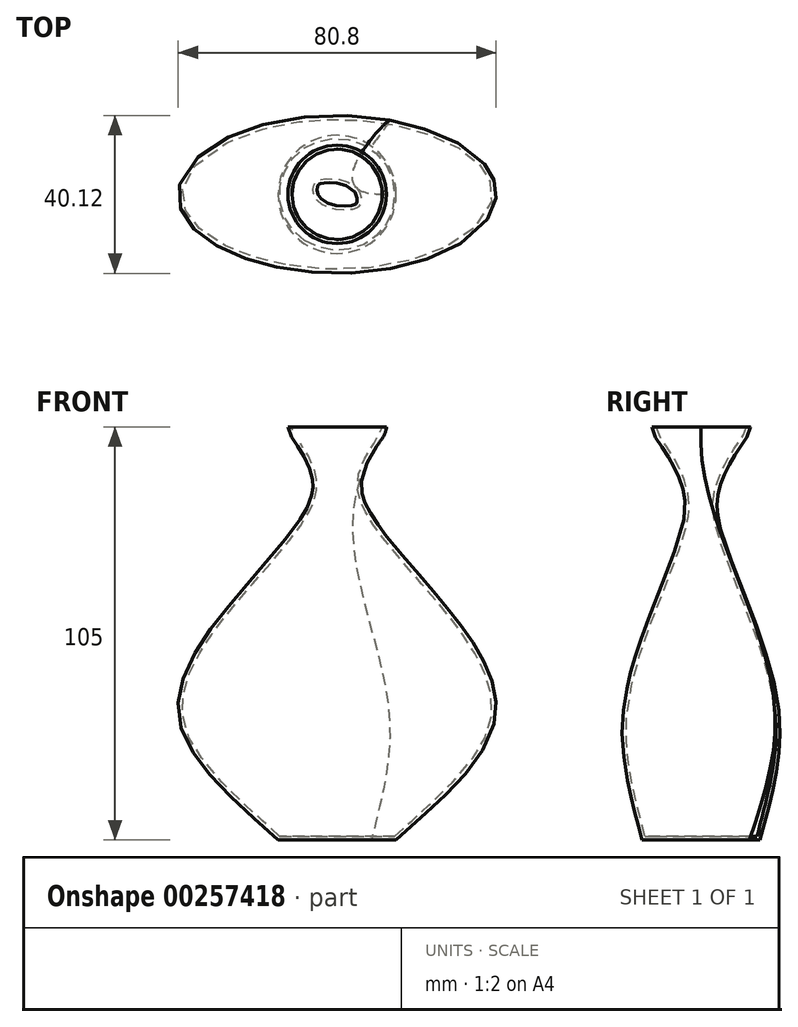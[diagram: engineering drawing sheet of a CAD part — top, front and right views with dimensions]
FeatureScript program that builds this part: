
annotation { "Feature Type Name" : "Feature", "Feature Type Description" : "" }
export const myFeature = defineFeature(function(context is Context, id is Id, definition is map)
    precondition{}
    {
        {
            var Q0;
            Q0=qCreatedBy(makeId("Top.planeOp"),FACE);
            var sketch = newSketch(context, id + "F0", { "sketchPlane" : qUnion([Q0])});
            skCircle(sketch, "E0", {"center": v(0, 0) * mm, "radius": 15 * mm});
            skSolve(sketch);
        }
        {
            var Q0;
            Q0=qCreatedBy(makeId("Top.planeOp"),FACE);
            cPlane(context, id + "F1", {"entities" : qUnion([Q0]), "cplaneType" : CPlaneType.OFFSET, "offset" : 30 * mm, "width" : 150 * mm, "height" : 150 * mm});
        }
        {
            var Q0;
            Q0=qCreatedBy(id+"F1.planeOp",FACE);
            var sketch = newSketch(context, id + "F2", { "sketchPlane" : qUnion([Q0])});
            skEllipse(sketch, "E1", {"center": v(0, 0) * mm, "majorRadius": 40 * mm, "minorRadius": 20 * mm, "majorAxis": v(1, 0)});
            skSolve(sketch);
        }
        {
            var Q0;
            Q0=qCreatedBy(id+"F1.planeOp",FACE);
            cPlane(context, id + "F3", {"entities" : qUnion([Q0]), "cplaneType" : CPlaneType.OFFSET, "offset" : 70 * mm, "width" : 150 * mm, "height" : 150 * mm});
        }
        {
            var Q0;
            Q0=qCreatedBy(id+"F3.planeOp",FACE);
            var sketch = newSketch(context, id + "F4", { "sketchPlane" : qUnion([Q0])});
            skCircle(sketch, "E2", {"center": v(0, 0) * mm, "radius": 10 * mm});
            skSolve(sketch);
        }
        {
            var Q0;
            Q0=qCreatedBy(id+"F3.planeOp",FACE);
            cPlane(context, id + "F5", {"entities" : qUnion([Q0]), "cplaneType" : CPlaneType.OFFSET, "offset" : 5 * mm, "width" : 150 * mm, "height" : 150 * mm});
        }
        {
            var Q0;
            Q0=qCreatedBy(id+"F5.planeOp",FACE);
            var sketch = newSketch(context, id + "F6", { "sketchPlane" : qUnion([Q0])});
            skCircle(sketch, "E3", {"center": v(0, 0) * mm, "radius": 12.5 * mm});
            skSolve(sketch);
        }
        {
            var Q0;
            Q0=makeQuery(id+"F6.imprint","IMPRINT",FACE,{"disambiguationData":[TD([[makeQuery(id+"F6.imprint","IMPRINT",EDGE,{"derivedFrom":sQuery(id+"F6.wireOp",EDGE,"E3")}),1.0]])]});
            var Q1;
            Q1=makeQuery(id+"F4.imprint","IMPRINT",FACE,{"disambiguationData":[TD([[makeQuery(id+"F4.imprint","IMPRINT",EDGE,{"derivedFrom":sQuery(id+"F4.wireOp",EDGE,"E2")}),1.0]])]});
            var Q2;
            Q2=makeQuery(id+"F2.imprint","IMPRINT",FACE,{"disambiguationData":[TD([[makeQuery(id+"F2.imprint","IMPRINT",EDGE,{"derivedFrom":sQuery(id+"F2.wireOp",EDGE,"E1")}),1.0]])]});
            var Q3;
            Q3=makeQuery(id+"F0.imprint","IMPRINT",FACE,{"disambiguationData":[TD([[makeQuery(id+"F0.imprint","IMPRINT",EDGE,{"derivedFrom":sQuery(id+"F0.wireOp",EDGE,"E0")}),1.0]])]});
            loft(context, id + "F7", {"startCondition" : LoftEndDerivativeType.NORMAL_TO_PROFILE, "startMagnitude" : 1, "sheetProfilesArray" : [{ "sheetProfileEntities" : qUnion([Q0]) }, { "sheetProfileEntities" : qUnion([Q1]) }, { "sheetProfileEntities" : qUnion([Q2]) }, { "sheetProfileEntities" : qUnion([Q3]) }]});
        }
        {
            var Q0;
            Q0=makeQuery(id+"F7.opLoft","CAP_FACE",FACE,{"disambiguationData":[OSD([makeQuery(id+"F6.imprint","IMPRINT",FACE,{"disambiguationData":[TD([[makeQuery(id+"F6.imprint","IMPRINT",EDGE,{"derivedFrom":sQuery(id+"F6.wireOp",EDGE,"E3")}),1.0]])]})])],"isStart":true});
            var Q1;
            Q1=makeQuery(id+"F7.opLoft","SWEPT_BODY",BODY,{"disambiguationData":[OSD([makeQuery(id+"F0.imprint","IMPRINT",FACE,{"disambiguationData":[TD([[makeQuery(id+"F0.imprint","IMPRINT",EDGE,{"derivedFrom":sQuery(id+"F0.wireOp",EDGE,"E0")}),1.0]])]}),sQuery(id+"F2.wireOp",EDGE,"E1"),sQuery(id+"F4.wireOp",EDGE,"E2"),makeQuery(id+"F6.imprint","IMPRINT",FACE,{"disambiguationData":[TD([[makeQuery(id+"F6.imprint","IMPRINT",EDGE,{"derivedFrom":sQuery(id+"F6.wireOp",EDGE,"E3")}),1.0]])]})])]});
            shell(context, id + "F8", {"entities" : qUnion([Q0]), "parts" : qUnion([Q1]), "thickness" : 1 * mm});
        }
    });
